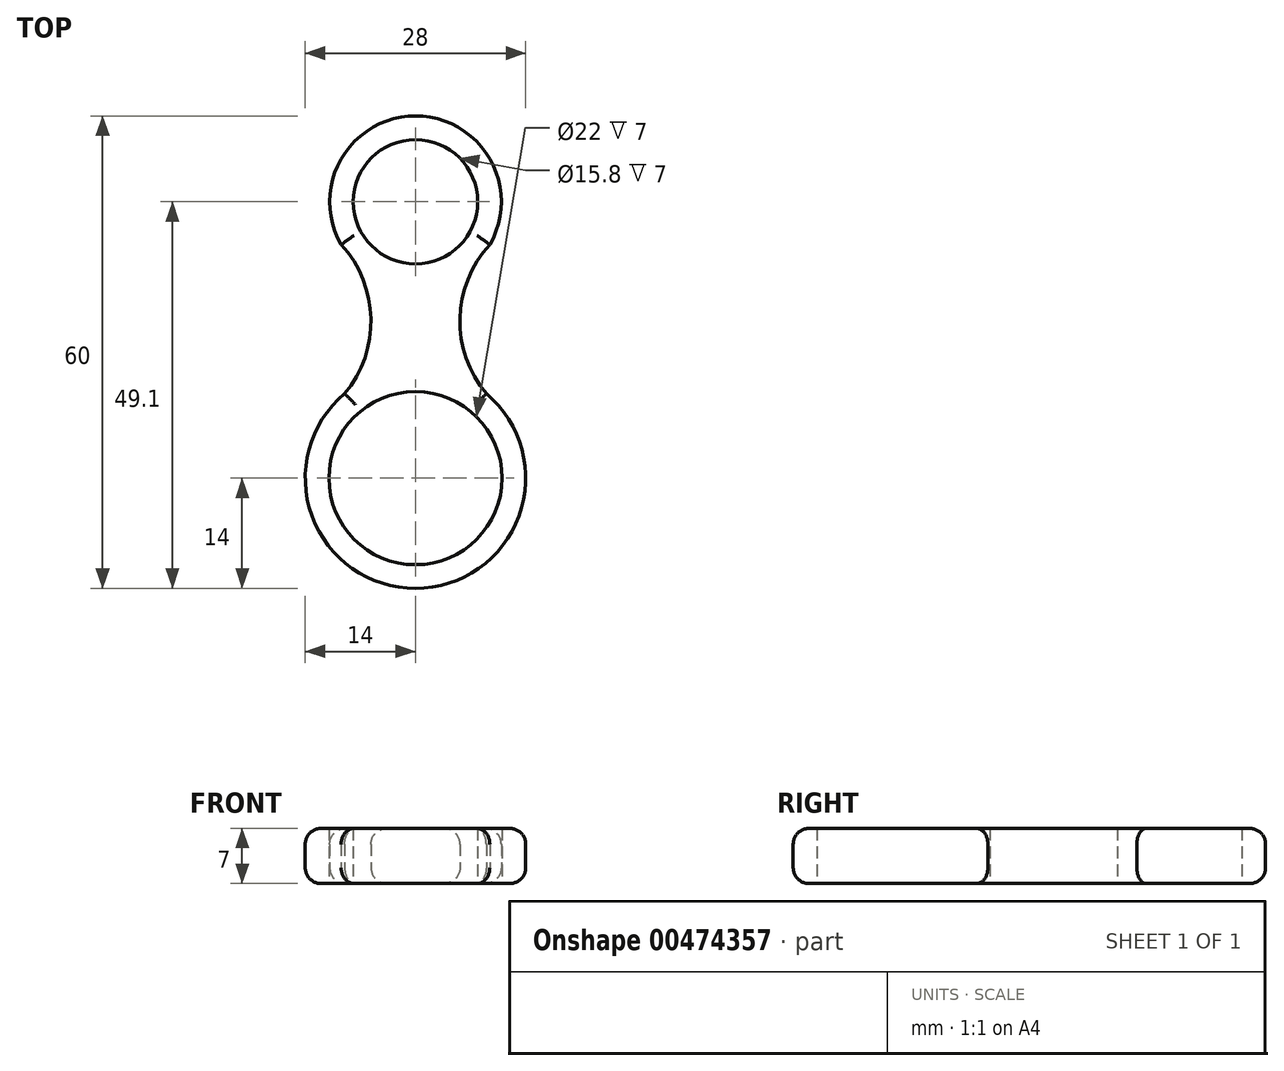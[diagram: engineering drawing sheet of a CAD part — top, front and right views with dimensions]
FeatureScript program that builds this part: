
annotation { "Feature Type Name" : "Feature", "Feature Type Description" : "" }
export const myFeature = defineFeature(function(context is Context, id is Id, definition is map)
    precondition{}
    {
        {
            var Q0;
            Q0=qCreatedBy(makeId("Top.planeOp"),FACE);
            var sketch = newSketch(context, id + "F0", { "sketchPlane" : qUnion([Q0])});
            skCircle(sketch, "E0", {"center": v(0, 0) * mm, "radius": 11 * mm});
            skArc(sketch, "E1", {"start": v(-9, 10.72) * mm, "mid": v(0, -14) * mm, "end": v(9, 10.72) * mm});
            skCircle(sketch, "E2", {"center": v(0, 35.1) * mm, "radius": 7.9 * mm});
            skArc(sketch, "E3", {"start": v(9.44, 29.65) * mm, "mid": v(0, 46) * mm, "end": v(-9.44, 29.65) * mm});
            skLineSegment(sketch, "E4", {"start": v(0, 35.1) * mm, "end": v(0, 0) * mm, "construction": true});
            skLineSegment(sketch, "E5", {"start": v(0, 35.1) * mm, "end": v(9.44, 29.65) * mm, "construction": true});
            skLineSegment(sketch, "E6", {"start": v(0, 0) * mm, "end": v(9, 10.72) * mm, "construction": true});
            skLineSegment(sketch, "E7", {"start": v(0, 0) * mm, "end": v(-9, 10.72) * mm, "construction": true});
            skLineSegment(sketch, "E8", {"start": v(0, 35.1) * mm, "end": v(-9.44, 29.65) * mm, "construction": true});
            skLineSegment(sketch, "E9", {"start": v(-9, -14) * mm, "end": v(9, -14) * mm, "construction": true});
            skLineSegment(sketch, "E10", {"start": v(-9, 46) * mm, "end": v(9, 46) * mm, "construction": true});
            skArc(sketch, "E11", {"start": v(9.44, 29.65) * mm, "mid": v(5.66, 20.27) * mm, "end": v(9, 10.72) * mm});
            skArc(sketch, "E12", {"start": v(-9, 10.72) * mm, "mid": v(-5.66, 20.27) * mm, "end": v(-9.44, 29.65) * mm});
            skPoint(sketch, "E13.visualSharp", {"position": v(-9.44, 29.65) * mm});
            skPoint(sketch, "E14.visualSharp", {"position": v(-9, 10.72) * mm});
            skPoint(sketch, "E15.visualSharp", {"position": v(9, 10.72) * mm});
            skPoint(sketch, "E16.visualSharp", {"position": v(9.44, 29.65) * mm});
            skSolve(sketch);
        }
        {
            var Q0;
            Q0 = qSketchRegion(id + "F0", true);
            extrude(context, id + "F1", {"entities" : qUnion([Q0]), "depth" : 7 * mm});
        }
        {
            var Q0;
            Q0=makeQuery(id+"F1.opExtrude","CAP_EDGE",EDGE,{"disambiguationData":[OSD([sQuery(id+"F0.wireOp",EDGE,"E12")])],"isStart":false});
            var Q1;
            Q1=makeQuery(id+"F1.opExtrude","CAP_EDGE",EDGE,{"disambiguationData":[OSD([sQuery(id+"F0.wireOp",EDGE,"E3")])],"isStart":false});
            var Q2;
            Q2=makeQuery(id+"F1.opExtrude","CAP_EDGE",EDGE,{"disambiguationData":[OSD([sQuery(id+"F0.wireOp",EDGE,"E11")])],"isStart":false});
            var Q3;
            Q3=makeQuery(id+"F1.opExtrude","CAP_EDGE",EDGE,{"disambiguationData":[OSD([sQuery(id+"F0.wireOp",EDGE,"E1")])],"isStart":false});
            var Q4;
            Q4=makeQuery(id+"F1.opExtrude","CAP_EDGE",EDGE,{"disambiguationData":[OSD([sQuery(id+"F0.wireOp",EDGE,"E1")])],"isStart":true});
            var Q5;
            Q5=makeQuery(id+"F1.opExtrude","CAP_EDGE",EDGE,{"disambiguationData":[OSD([sQuery(id+"F0.wireOp",EDGE,"E11")])],"isStart":true});
            var Q6;
            Q6=makeQuery(id+"F1.opExtrude","CAP_EDGE",EDGE,{"disambiguationData":[OSD([sQuery(id+"F0.wireOp",EDGE,"E3")])],"isStart":true});
            var Q7;
            Q7=makeQuery(id+"F1.opExtrude","CAP_EDGE",EDGE,{"disambiguationData":[OSD([sQuery(id+"F0.wireOp",EDGE,"E12")])],"isStart":true});
            fillet(context, id + "F2", {"entities" : qUnion([Q0, Q1, Q2, Q3, Q4, Q5, Q6, Q7]), "radius" : 2 * mm, "tangentPropagation" : true, "allowEdgeOverflow" : false});
        }
    });
